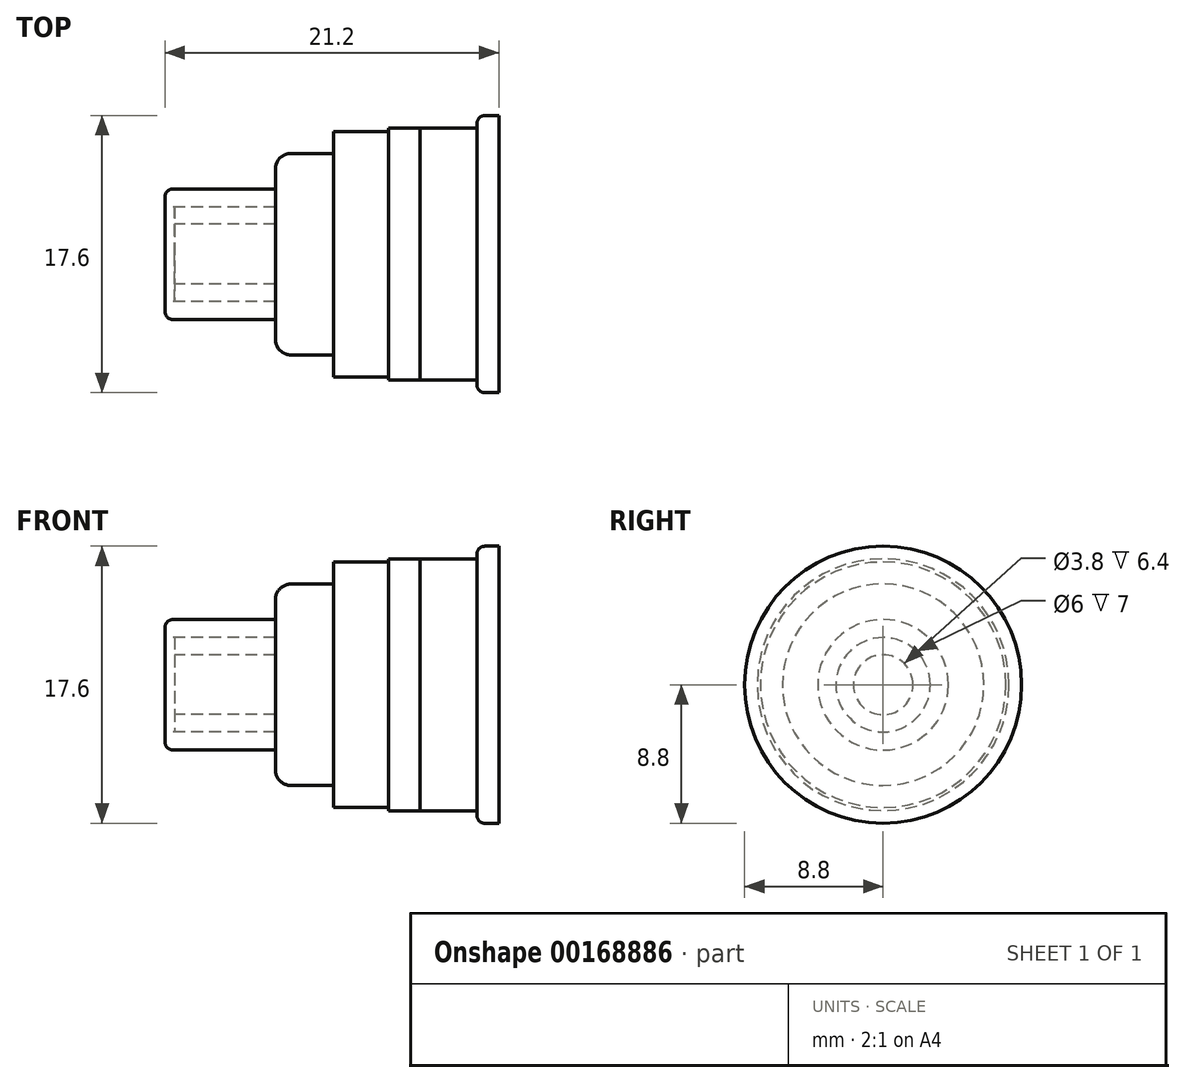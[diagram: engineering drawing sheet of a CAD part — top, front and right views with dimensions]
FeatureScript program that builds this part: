
annotation { "Feature Type Name" : "Feature", "Feature Type Description" : "" }
export const myFeature = defineFeature(function(context is Context, id is Id, definition is map)
    precondition{}
    {
        {
            var Q0;
            Q0=qCreatedBy(makeId("Front.planeOp"),FACE);
            var sketch = newSketch(context, id + "F0", { "sketchPlane" : qUnion([Q0])});
            skLineSegment(sketch, "E0", {"start": v(0, 7.8) * mm, "end": v(-3.5, 7.8) * mm});
            skLineSegment(sketch, "E1", {"start": v(-3.5, 7.8) * mm, "end": v(-3.5, 0) * mm});
            skLineSegment(sketch, "E2", {"start": v(-3.5, 0) * mm, "end": v(0, 0) * mm});
            skLineSegment(sketch, "E3", {"start": v(0, 0) * mm, "end": v(0, 7.8) * mm});
            skLineSegment(sketch, "E4", {"start": v(-3.5, 6.4) * mm, "end": v(-6.2, 6.4) * mm});
            skLineSegment(sketch, "E5", {"start": v(-7.2, 5.4) * mm, "end": v(-7.2, 0) * mm});
            skLineSegment(sketch, "E6", {"start": v(-7.2, 0) * mm, "end": v(-3.5, 0) * mm});
            skLineSegment(sketch, "E7", {"start": v(-7.2, 4.15) * mm, "end": v(-13.7, 4.15) * mm});
            skLineSegment(sketch, "E8", {"start": v(-14.2, 3.65) * mm, "end": v(-14.2, 3) * mm});
            skLineSegment(sketch, "E9", {"start": v(-14.2, 3) * mm, "end": v(-7.2, 3) * mm});
            skLineSegment(sketch, "E10", {"start": v(0, 7.8) * mm, "end": v(0, 8) * mm});
            skLineSegment(sketch, "E11", {"start": v(0, 8) * mm, "end": v(2, 8) * mm});
            skLineSegment(sketch, "E12", {"start": v(2, 8) * mm, "end": v(2, 0) * mm});
            skLineSegment(sketch, "E13", {"start": v(2, 0) * mm, "end": v(0, 0) * mm});
            skLineSegment(sketch, "E14", {"start": v(2, 8) * mm, "end": v(5.6, 8) * mm});
            skLineSegment(sketch, "E15", {"start": v(5.6, 8) * mm, "end": v(5.6, 8.3) * mm});
            skLineSegment(sketch, "E16", {"start": v(6.1, 8.8) * mm, "end": v(7, 8.8) * mm});
            skLineSegment(sketch, "E17", {"start": v(7, 8.8) * mm, "end": v(7, 0) * mm});
            skLineSegment(sketch, "E18", {"start": v(7, 0) * mm, "end": v(2, 0) * mm});
            skLineSegment(sketch, "E19", {"start": v(-13.18, 0) * mm, "end": v(10.16, 0) * mm, "construction": true});
            skPoint(sketch, "E19.endSnap0", {"position": v(1, 0) * mm});
            skPoint(sketch, "E20.visualSharp", {"position": v(5.6, 8.8) * mm});
            skArc(sketch, "E20.filletArc", {"start": v(6.1, 8.8) * mm, "mid": v(5.75, 8.65) * mm, "end": v(5.6, 8.3) * mm});
            skPoint(sketch, "E21.visualSharp", {"position": v(-7.2, 6.4) * mm});
            skArc(sketch, "E21.filletArc", {"start": v(-6.2, 6.4) * mm, "mid": v(-6.9, 6.1) * mm, "end": v(-7.2, 5.4) * mm});
            skPoint(sketch, "E22.visualSharp", {"position": v(-14.2, 4.15) * mm});
            skArc(sketch, "E22.filletArc", {"start": v(-13.7, 4.15) * mm, "mid": v(-14.05, 4) * mm, "end": v(-14.2, 3.65) * mm});
            skLineSegment(sketch, "E23", {"start": v(-13.6, 3) * mm, "end": v(-13.6, 1.9) * mm});
            skLineSegment(sketch, "E24", {"start": v(-13.6, 1.9) * mm, "end": v(-7.2, 1.9) * mm});
            skSolve(sketch);
        }
        {
            var Q0;
            {var subQ0=sQuery(id+"F0.wireOp",EDGE,"E7");Q0=makeQuery(id+"F0.imprint","IMPRINT",FACE,{"disambiguationData":[TD([[makeQuery(id+"F0.imprint","IMPRINT",EDGE,{"derivedFrom":subQ0}),1.0]])]});}
            var Q1;
            Q1=sQuery(id+"F0.wireOp",EDGE,"E19");
            revolve(context, id + "F1", {"entities" : qUnion([Q0]), "axis" : qUnion([Q1]), "revolveType" : RevolveType.FULL});
        }
        {
            var Q0;
            {var subQ3=sQuery(id+"F0.wireOp",EDGE,"E4");Q0=makeQuery(id+"F0.imprint","IMPRINT",FACE,{"disambiguationData":[TD([[makeQuery(id+"F0.imprint","IMPRINT",EDGE,{"derivedFrom":subQ3}),1.0]])]});}
            var Q1;
            Q1=sQuery(id+"F0.wireOp",EDGE,"E6");
            revolve(context, id + "F2", {"entities" : qUnion([Q0]), "axis" : qUnion([Q1]), "revolveType" : RevolveType.FULL});
        }
        {
            var Q0;
            {var subQ3=sQuery(id+"F0.wireOp",EDGE,"E0");Q0=makeQuery(id+"F0.imprint","IMPRINT",FACE,{"disambiguationData":[TD([[makeQuery(id+"F0.imprint","IMPRINT",EDGE,{"derivedFrom":subQ3}),1.0]])]});}
            var Q1;
            Q1=sQuery(id+"F0.wireOp",EDGE,"E2");
            revolve(context, id + "F3", {"entities" : qUnion([Q0]), "axis" : qUnion([Q1]), "revolveType" : RevolveType.FULL});
        }
        {
            var Q0;
            Q0=makeQuery(id+"F0.imprint","IMPRINT",FACE,{"disambiguationData":[TD([[makeQuery(id+"F0.imprint","IMPRINT",EDGE,{"derivedFrom":sQuery(id+"F0.wireOp",EDGE,"E3")}),-1.0]])]});
            var Q1;
            Q1=sQuery(id+"F0.wireOp",EDGE,"E18");
            revolve(context, id + "F4", {"entities" : qUnion([Q0]), "axis" : qUnion([Q1]), "revolveType" : RevolveType.FULL});
        }
        {
            var Q0;
            {var subQ4=sQuery(id+"F0.wireOp",EDGE,"E23");Q0=makeQuery(id+"F0.imprint","IMPRINT",FACE,{"disambiguationData":[TD([[makeQuery(id+"F0.imprint","IMPRINT",EDGE,{"derivedFrom":subQ4}),1.0]])]});}
            var Q1;
            Q1=sQuery(id+"F0.wireOp",EDGE,"E19");
            revolve(context, id + "F5", {"entities" : qUnion([Q0]), "axis" : qUnion([Q1]), "revolveType" : RevolveType.FULL});
        }
        {
            var Q0;
            Q0=makeQuery(id+"F0.imprint","IMPRINT",FACE,{"disambiguationData":[TD([[makeQuery(id+"F0.imprint","IMPRINT",EDGE,{"derivedFrom":sQuery(id+"F0.wireOp",EDGE,"E12")}),1.0]])]});
            var Q1;
            Q1=sQuery(id+"F0.wireOp",EDGE,"E19");
            revolve(context, id + "F6", {"entities" : qUnion([Q0]), "axis" : qUnion([Q1]), "revolveType" : RevolveType.FULL});
        }
    });
